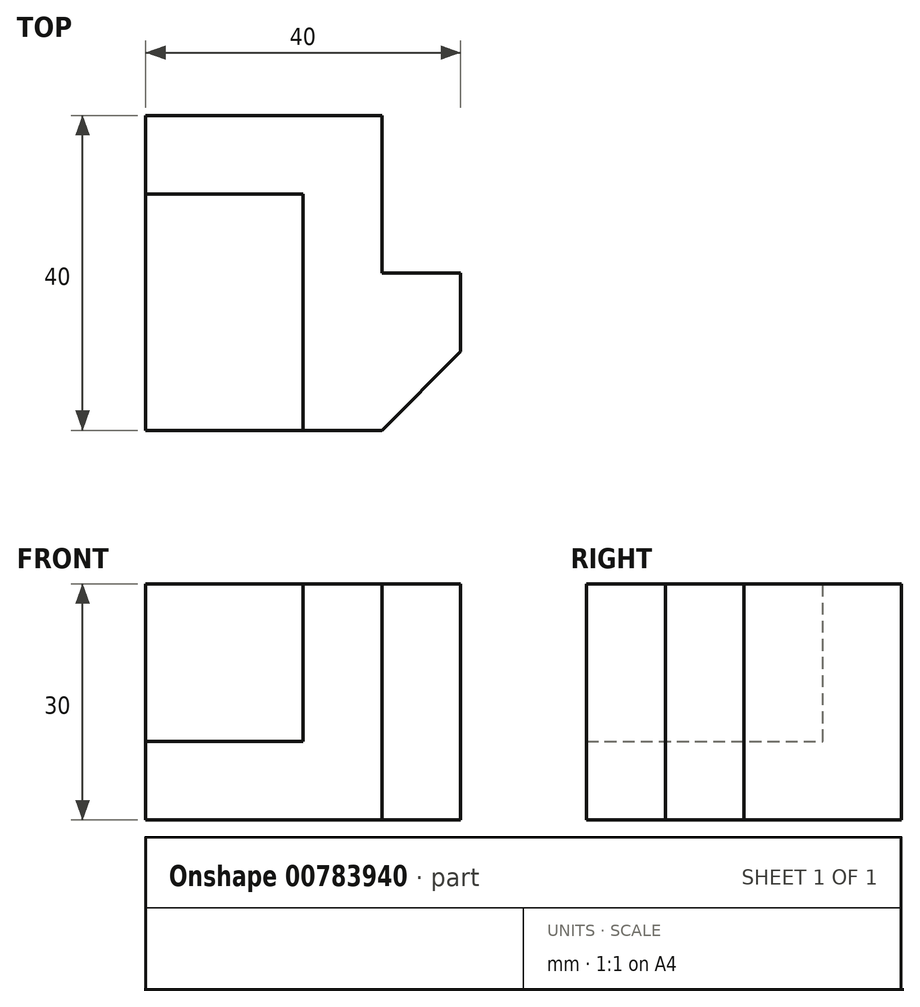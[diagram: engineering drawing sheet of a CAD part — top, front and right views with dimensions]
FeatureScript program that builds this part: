
annotation { "Feature Type Name" : "Feature", "Feature Type Description" : "" }
export const myFeature = defineFeature(function(context is Context, id is Id, definition is map)
    precondition{}
    {
        {
            var Q0;
            Q0=qCreatedBy(makeId("Top.planeOp"),FACE);
            var sketch = newSketch(context, id + "F0", { "sketchPlane" : qUnion([Q0])});
            skLineSegment(sketch, "E0", {"start": v(0, 0) * mm, "end": v(40, 0) * mm});
            skLineSegment(sketch, "E1", {"start": v(40, 0) * mm, "end": v(0, 0) * mm});
            skLineSegment(sketch, "E2", {"start": v(0, 0) * mm, "end": v(0, 40) * mm});
            skLineSegment(sketch, "E3", {"start": v(0, 0) * mm, "end": v(0, 30) * mm});
            skLineSegment(sketch, "E4", {"start": v(0, 30) * mm, "end": v(20, 30) * mm});
            skLineSegment(sketch, "E5", {"start": v(0, 40) * mm, "end": v(30, 40) * mm});
            skLineSegment(sketch, "E6", {"start": v(30, 40) * mm, "end": v(30, 20) * mm});
            skLineSegment(sketch, "E7", {"start": v(30, 20) * mm, "end": v(40, 20) * mm});
            skLineSegment(sketch, "E8", {"start": v(40, 20) * mm, "end": v(40, 10) * mm});
            skLineSegment(sketch, "E9", {"start": v(0, 0) * mm, "end": v(30, 0) * mm});
            skLineSegment(sketch, "E10", {"start": v(40, 10) * mm, "end": v(30, 0) * mm});
            skLineSegment(sketch, "E11", {"start": v(20, 30) * mm, "end": v(20, 0) * mm});
            skLineSegment(sketch, "E12", {"start": v(20, 0) * mm, "end": v(0, 0) * mm});
            skLineSegment(sketch, "E13", {"start": v(20, 10) * mm, "end": v(0, 10) * mm});
            skSolve(sketch);
        }
        {
            var Q0;
            {var subQ5=sQuery(id+"F0.wireOp",EDGE,"E13");Q0=makeQuery(id+"F0.imprint","IMPRINT",FACE,{"disambiguationData":[TD([[makeQuery(id+"F0.imprint","IMPRINT",EDGE,{"derivedFrom":subQ5}),1.0]])]});}
            var Q1;
            {var subQ2=sQuery(id+"F0.wireOp",EDGE,"E4");Q1=makeQuery(id+"F0.imprint","IMPRINT",FACE,{"disambiguationData":[TD([[makeQuery(id+"F0.imprint","IMPRINT",EDGE,{"derivedFrom":subQ2}),-1.0]])]});}
            var Q2;
            {var subQ0=sQuery(id+"F0.wireOp",EDGE,"E4");Q2=makeQuery(id+"F0.imprint","IMPRINT",FACE,{"disambiguationData":[TD([[makeQuery(id+"F0.imprint","IMPRINT",EDGE,{"derivedFrom":subQ0}),1.0]])]});}
            extrude(context, id + "F1", {"entities" : qUnion([Q0, Q1, Q2]), "depth" : 30 * mm, "offsetDistance" : 25 * mm});
        }
        {
            var Q0;
            Q0=makeQuery(id+"F1.opExtrude","CAP_FACE",FACE,{"disambiguationData":[OSD([sQuery(id+"F0.wireOp",EDGE,"E0"),sQuery(id+"F0.wireOp",EDGE,"E2"),sQuery(id+"F0.wireOp",EDGE,"E5"),sQuery(id+"F0.wireOp",EDGE,"E6"),sQuery(id+"F0.wireOp",EDGE,"E7"),sQuery(id+"F0.wireOp",EDGE,"E8"),sQuery(id+"F0.wireOp",EDGE,"E10")])],"isStart":false});
            var sketch = newSketch(context, id + "F2", { "sketchPlane" : qUnion([Q0])});
            skLineSegment(sketch, "E14", {"start": v(0, 40) * mm, "end": v(0, 0) * mm});
            skLineSegment(sketch, "E15", {"start": v(0, 0) * mm, "end": v(30, 0) * mm});
            skLineSegment(sketch, "E16", {"start": v(0, 0) * mm, "end": v(20, 0) * mm});
            skLineSegment(sketch, "E17", {"start": v(0, 0) * mm, "end": v(0, 30) * mm});
            skLineSegment(sketch, "E18", {"start": v(0, 30) * mm, "end": v(20, 30) * mm});
            skLineSegment(sketch, "E19", {"start": v(20, 30) * mm, "end": v(20, 0) * mm});
            skLineSegment(sketch, "E20", {"start": v(0, 0) * mm, "end": v(0, 10) * mm});
            skLineSegment(sketch, "E21", {"start": v(0, 10) * mm, "end": v(20, 10) * mm});
            skLineSegment(sketch, "E22", {"start": v(20, 10) * mm, "end": v(20, 0) * mm});
            skSolve(sketch);
        }
        {
            var Q0;
            Q0=makeQuery(id+"F2.imprint","IMPRINT",FACE,{"disambiguationData":[TD([[makeQuery(id+"F2.imprint","IMPRINT",EDGE,{"derivedFrom":sQuery(id+"F2.wireOp",EDGE,"E14")}),-1.0]])]});
            extrude(context, id + "F3", {"entities" : qUnion([Q0]), "operationType" : NewBodyOperationType.REMOVE, "oppositeDirection" : true, "depth" : 20 * mm, "offsetDistance" : 25 * mm});
        }
        {
            var Q0;
            Q0=makeQuery(id+"F3.boolean.opBoolean","COPY",FACE,{"derivedFrom":makeQuery(id+"F3.opExtrude","SWEPT_FACE",FACE,{"disambiguationData":[OSD([sQuery(id+"F2.wireOp",EDGE,"E19"),sQuery(id+"F2.wireOp",EDGE,"E22")])]})});
            var sketch = newSketch(context, id + "F4", { "sketchPlane" : qUnion([Q0])});
            skLineSegment(sketch, "E23", {"start": v(0, 30) * mm, "end": v(0, 20) * mm});
            skLineSegment(sketch, "E24", {"start": v(0, 30) * mm, "end": v(30, 30) * mm});
            skLineSegment(sketch, "E25", {"start": v(0, 20) * mm, "end": v(10, 30) * mm});
            skSolve(sketch);
        }
        {
            var Q0;
            Q0 = qSketchRegion(id + "F4", true);
            extrude(context, id + "F5", {"entities" : qUnion([Q0]), "operationType" : NewBodyOperationType.REMOVE, "oppositeDirection" : true, "depth" : 25 * mm, "offsetDistance" : 25 * mm});
        }
    });
